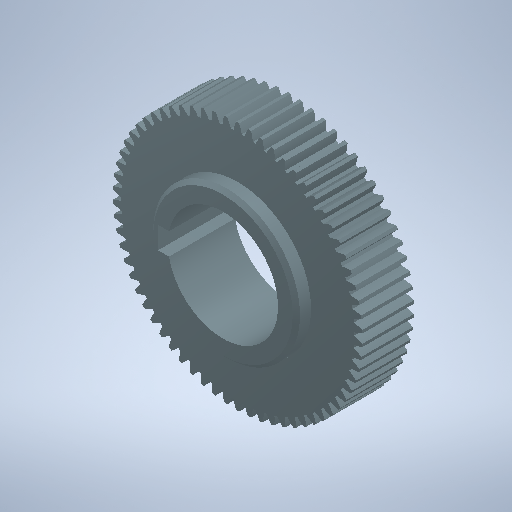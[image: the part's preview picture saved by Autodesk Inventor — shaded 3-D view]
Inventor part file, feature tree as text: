
AUTODESK INVENTOR PART (.ipt)
format: ipt  version: 2025 (Build 290162010, 162A)  size: 560,640 bytes
history: native  units: mm (DEFAULTED — no unit token found)
features: sketch x5, extrude x3, plane x3, other x3, chamfer x1, hole x1
ambient origin geometry x8: Origin, YZ Plane, XZ Plane, XY Plane, X Axis, Y Axis, Z Axis, Center Point
bodies: Body1 (feature_tree), Body2 (feature_tree)
feature tree (16):
  extrude  "Extrusion1"  Depth=7.0mm TaperAngle=0.0deg
  plane  "Work Plane2"
  plane  "Work Plane8"
  plane  "Work Plane9"
  other  "Stirnzahnrad"
  sketch  "Skizze4"  dims[d3=33.0mm d4=10.0mm d5=0.0mm]
  extrude  "Extrusion2"  Depth=10.0mm TaperAngle=0.0deg
  chamfer  "Fasen1"  Distance=0.475999mm
  hole  "Bohrung1"  [1 undecoded]
  extrude  "Extrusion4"  Depth=10.0mm
  sketch  "Sketch1"  dims[d0=34.0mm d1=7.0mm d2=0.0mm]
  other  "Srf1"
  sketch  "Skizze5"  dims[d16=33.0mm d17=0.0mm d34=0.475999mm]
  sketch  "Skizze6"  dims[d39=0.0mm d41=0.0mm]
  sketch  "Skizze7"  dims[d43=33.0mm d46=33.0mm d47=0.0mm d48=0.0mm d50=33.0mm d51=20.0mm d52=2.0mm d53=0.0mm d54=0.5mm d55=2.0mm d56=45.0deg d57=15.0mm d58=6.0mm d59=4.0mm d60=2.0mm d61=90.0deg d62=8.0mm d63=0.0mm d70=3.0mm d71=8.85mm d72=10.0mm d73=0.0mm]
  other  "Flankendurchmesser"
note: 1 required parameter value undecoded (feature->parameter linkage not recoverable at this tier; creation-order binding heuristic only, values carry confidence <= 0.55)
